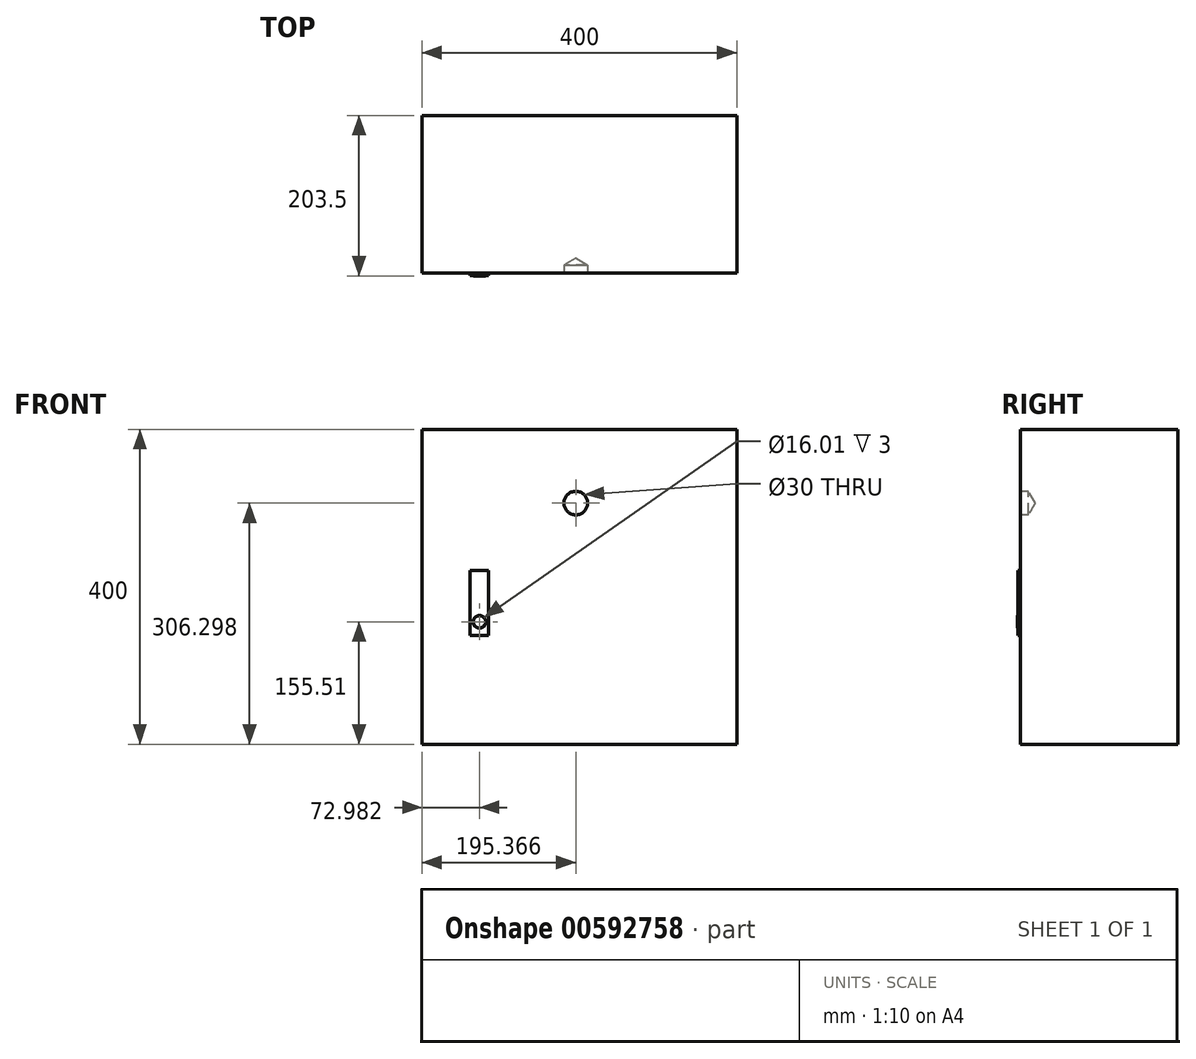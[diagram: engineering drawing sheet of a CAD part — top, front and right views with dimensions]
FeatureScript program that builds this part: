
annotation { "Feature Type Name" : "Feature", "Feature Type Description" : "" }
export const myFeature = defineFeature(function(context is Context, id is Id, definition is map)
    precondition{}
    {
        {
            var Q0;
            Q0=qCreatedBy(makeId("Front.planeOp"),FACE);
            var sketch = newSketch(context, id + "F0", { "sketchPlane" : qUnion([Q0])});
            skLineSegment(sketch, "E0.bottom", {"start": v(-61.17, 356.33) * mm, "end": v(338.83, 356.33) * mm});
            skLineSegment(sketch, "E0.top", {"start": v(-61.17, -43.67) * mm, "end": v(338.83, -43.67) * mm});
            skLineSegment(sketch, "E0.left", {"start": v(-61.17, 356.33) * mm, "end": v(-61.17, -43.67) * mm});
            skLineSegment(sketch, "E0.right", {"start": v(338.83, 356.33) * mm, "end": v(338.83, -43.67) * mm});
            skSolve(sketch);
        }
        {
            var Q0;
            Q0=makeQuery(id+"F0.imprint","IMPRINT",FACE,{"disambiguationData":[TD([[makeQuery(id+"F0.imprint","IMPRINT",EDGE,{"derivedFrom":sQuery(id+"F0.wireOp",EDGE,"E0.bottom")}),-1.0]])]});
            extrude(context, id + "F1", {"entities" : qUnion([Q0]), "depth" : 200 * mm, "offsetDistance" : 25 * mm});
        }
        {
            var Q0;
            Q0=makeQuery(id+"F1.opExtrude","CAP_FACE",FACE,{"disambiguationData":[OSD([sQuery(id+"F0.wireOp",EDGE,"E0.bottom"),sQuery(id+"F0.wireOp",EDGE,"E0.top"),sQuery(id+"F0.wireOp",EDGE,"E0.left"),sQuery(id+"F0.wireOp",EDGE,"E0.right")])],"isStart":false});
            var sketch = newSketch(context, id + "F2", { "sketchPlane" : qUnion([Q0])});
            skLineSegment(sketch, "E1.bottom", {"start": v(0, 176.93) * mm, "end": v(23.62, 176.93) * mm});
            skLineSegment(sketch, "E1.top", {"start": v(0, 94.43) * mm, "end": v(23.62, 94.43) * mm});
            skLineSegment(sketch, "E1.left", {"start": v(0, 176.93) * mm, "end": v(0, 94.43) * mm});
            skLineSegment(sketch, "E1.right", {"start": v(23.62, 176.93) * mm, "end": v(23.62, 94.43) * mm});
            skCircle(sketch, "E2", {"center": v(11.81, 111.84) * mm, "radius": 8 * mm});
            skPoint(sketch, "E2.centerSnap0", {"position": v(11.81, 94.43) * mm});
            skCircle(sketch, "E3", {"center": v(11.81, 111.84) * mm, "radius": 7.75 * mm});
            skSolve(sketch);
        }
        {
            var Q0;
            Q0=makeQuery(id+"F2.imprint","IMPRINT",FACE,{"disambiguationData":[TD([[makeQuery(id+"F2.imprint","IMPRINT",EDGE,{"derivedFrom":sQuery(id+"F2.wireOp",EDGE,"E1.bottom")}),-1.0]])]});
            extrude(context, id + "F3", {"entities" : qUnion([Q0]), "operationType" : NewBodyOperationType.ADD, "depth" : 3 * mm, "offsetDistance" : 25 * mm});
        }
        {
            var Q0;
            Q0=makeQuery(id+"F2.imprint","IMPRINT",FACE,{"disambiguationData":[TD([[makeQuery(id+"F2.imprint","IMPRINT",EDGE,{"derivedFrom":sQuery(id+"F2.wireOp",EDGE,"E3")}),1.0]])]});
            extrude(context, id + "F4", {"entities" : qUnion([Q0]), "operationType" : NewBodyOperationType.ADD, "depth" : 3.5 * mm, "offsetDistance" : 25 * mm});
        }
        {
            var Q0;
            Q0=makeQuery(id+"F2.imprint","IMPRINT",FACE,{"disambiguationData":[TD([[makeQuery(id+"F2.imprint","IMPRINT",EDGE,{"derivedFrom":sQuery(id+"F2.wireOp",EDGE,"E1.bottom")}),1.0]])]});
            var sketch = newSketch(context, id + "F5", { "sketchPlane" : qUnion([Q0])});
            skCircle(sketch, "E4", {"center": v(134.2, 262.63) * mm, "radius": 15 * mm});
            skSolve(sketch);
        }
        {
            var Q0;
            Q0=sQuery(id+"F5.wireOp",VERTEX,"E4.center");
            var Q1;
            Q1=makeQuery(id+"F1.opExtrude","SWEPT_BODY",BODY,{"disambiguationData":[OSD([sQuery(id+"F0.wireOp",EDGE,"E0.bottom"),sQuery(id+"F0.wireOp",EDGE,"E0.top"),sQuery(id+"F0.wireOp",EDGE,"E0.left"),sQuery(id+"F0.wireOp",EDGE,"E0.right")])]});
            hole(context, id + "F6", {"style" : HoleStyle.SIMPLE, "endStyle" : HoleEndStyle.BLIND, "holeDiameter" : 30 * mm, "majorDiameter" : 5 * mm, "holeDepth" : 10 * mm, "isTappedThrough" : true, "tappedDepth" : 12 * mm, "tapClearance" : 3, "locations" : qUnion([Q0]), "scope" : qUnion([Q1])});
        }
    });
